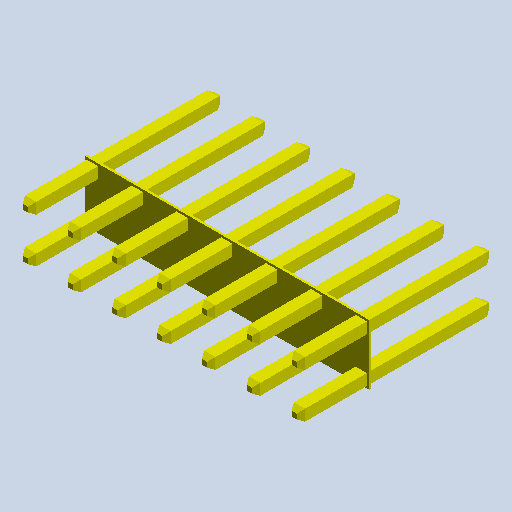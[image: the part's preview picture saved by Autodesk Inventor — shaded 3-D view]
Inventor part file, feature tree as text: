
AUTODESK INVENTOR PART (.ipt)
format: ipt  version: 2024.2 (Build 282272000, 272)  size: 368,128 bytes
history: native  units: mm (DEFAULTED — no unit token found)
features: other x14, extrude x10, sketch x10
ambient origin geometry x8: Origin, YZ Plane, XZ Plane, XY Plane, X Axis, Y Axis, Z Axis, Center Point
bodies: Solid1 (feature_tree)
feature tree (34):
  extrude  "Extrusion1"  Depth=16.129mm TaperAngle=0.0deg
  extrude  "Extrusion2"  Depth=10.16mm TaperAngle=0.0deg
  extrude  "Extrusion3"  Depth=35.56mm TaperAngle=0.0deg
  extrude  "Extrusion4"  Depth=35.56mm TaperAngle=0.0deg
  extrude  "Extrusion5"  Depth=10.16mm TaperAngle=0.0deg
  extrude  "Extrusion6"  [1 undecoded]
  extrude  "Extrusion7"  [1 undecoded]
  extrude  "Extrusion8"  [1 undecoded]
  extrude  "Extrusion9"  [1 undecoded]
  extrude  "Extrusion10"  [1 undecoded]
  other  "pin_XY"
  other  "pin_YZ"
  other  "pin_ZX"
  other  "pin_X"
  other  "pin_Y"
  other  "pin_Z"
  other  "pin_Center"
  other  "zst_prj_pin_XY"
  other  "zst_prj_pin_YZ"
  other  "zst_prj_pin_ZX"
  other  "zst_prj_pin_X"
  other  "zst_prj_pin_Y"
  other  "zst_prj_pin_Z"
  other  "zst_prj_pin_Center"
  sketch  "Sketch_1"  dims[d0=3.175mm d1=0.0mm d2=16.129mm d3=0.0mm]
  sketch  "Sketch_26"
  sketch  "Sketch_9"  dims[d4=10.16mm d5=0.0mm d6=10.16mm d7=0.0mm]
  sketch  "Sketch_12"  dims[d8=35.56mm d9=0.0mm d10=35.56mm d11=0.0mm]
  sketch  "Sketch_14"  dims[d12=35.56mm d13=0.0mm d14=35.56mm d15=0.0mm]
  sketch  "Sketch_16"  dims[d16=10.16mm d17=0.0mm d18=10.16mm d19=0.0mm]
  sketch  "Sketch_40"
  sketch  "Sketch_44"
  sketch  "Sketch_45"
  sketch  "Sketch_46"
note: 5 required parameter values undecoded (feature->parameter linkage not recoverable at this tier; creation-order binding heuristic only, values carry confidence <= 0.55)
